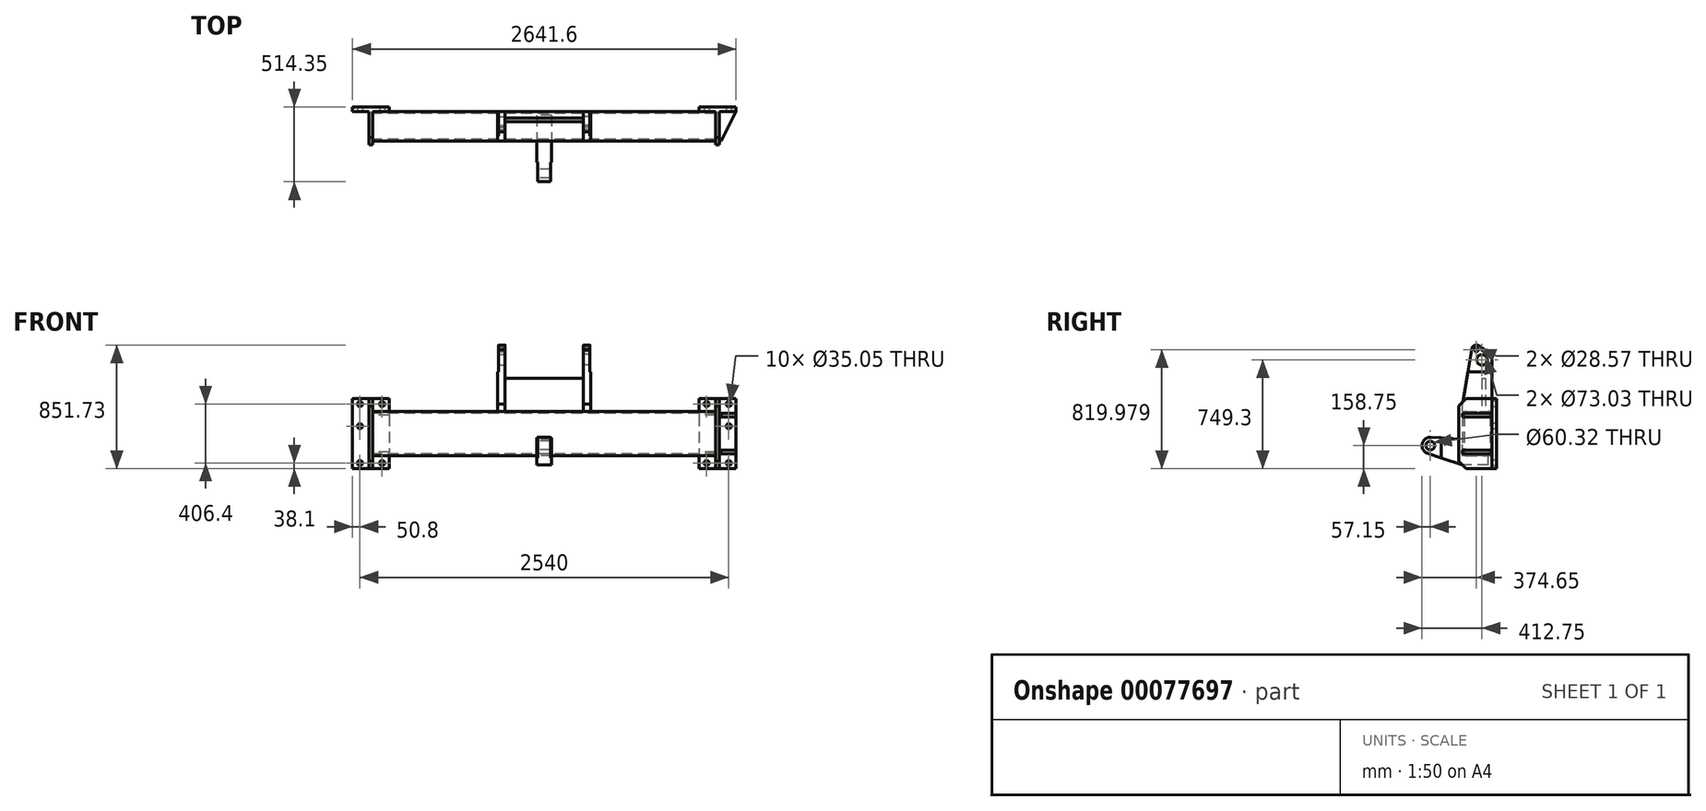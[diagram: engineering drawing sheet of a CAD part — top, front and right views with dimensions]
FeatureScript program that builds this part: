
annotation { "Feature Type Name" : "Feature", "Feature Type Description" : "" }
export const myFeature = defineFeature(function(context is Context, id is Id, definition is map)
    precondition{}
    {
        {
            var Q0;
            Q0=qCreatedBy(makeId("Right.planeOp"),FACE);
            var sketch = newSketch(context, id + "F0", { "sketchPlane" : qUnion([Q0])});
            skLineSegment(sketch, "E0.bottom", {"start": v(-76.2, 152.4) * mm, "end": v(76.2, 152.4) * mm});
            skLineSegment(sketch, "E0.top", {"start": v(-76.2, -152.4) * mm, "end": v(76.2, -152.4) * mm});
            skLineSegment(sketch, "E0.left", {"start": v(-101.6, 127) * mm, "end": v(-101.6, -127) * mm});
            skLineSegment(sketch, "E0.right", {"start": v(101.6, 127) * mm, "end": v(101.6, -127) * mm});
            skPoint(sketch, "E0.middle", {"position": v(0, 0) * mm});
            skPoint(sketch, "E1.visualSharp", {"position": v(-101.6, 152.4) * mm});
            skArc(sketch, "E1.filletArc", {"start": v(-76.2, 152.4) * mm, "mid": v(-94.16, 144.96) * mm, "end": v(-101.6, 127) * mm});
            skPoint(sketch, "E2.visualSharp", {"position": v(101.6, 152.4) * mm});
            skArc(sketch, "E2.filletArc", {"start": v(101.6, 127) * mm, "mid": v(94.16, 144.96) * mm, "end": v(76.2, 152.4) * mm});
            skPoint(sketch, "E3.visualSharp", {"position": v(101.6, -152.4) * mm});
            skArc(sketch, "E3.filletArc", {"start": v(76.2, -152.4) * mm, "mid": v(94.16, -144.96) * mm, "end": v(101.6, -127) * mm});
            skPoint(sketch, "E4.visualSharp", {"position": v(-101.6, -152.4) * mm});
            skArc(sketch, "E4.filletArc", {"start": v(-101.6, -127) * mm, "mid": v(-94.16, -144.96) * mm, "end": v(-76.2, -152.4) * mm});
            skArc(sketch, "E5.0", {"start": v(-76.2, 139.7) * mm, "mid": v(-85.18, 135.98) * mm, "end": v(-88.9, 127) * mm});
            skLineSegment(sketch, "E5.1", {"start": v(-88.9, 127) * mm, "end": v(-88.9, -127) * mm});
            skLineSegment(sketch, "E5.2", {"start": v(-76.2, 139.7) * mm, "end": v(76.2, 139.7) * mm});
            skArc(sketch, "E5.3", {"start": v(-88.9, -127) * mm, "mid": v(-85.18, -135.98) * mm, "end": v(-76.2, -139.7) * mm});
            skArc(sketch, "E5.4", {"start": v(88.9, 127) * mm, "mid": v(85.18, 135.98) * mm, "end": v(76.2, 139.7) * mm});
            skLineSegment(sketch, "E5.5", {"start": v(88.9, 127) * mm, "end": v(88.9, -127) * mm});
            skArc(sketch, "E5.6", {"start": v(76.2, -139.7) * mm, "mid": v(85.18, -135.98) * mm, "end": v(88.9, -127) * mm});
            skLineSegment(sketch, "E5.7", {"start": v(-76.2, -139.7) * mm, "end": v(76.2, -139.7) * mm});
            skSolve(sketch);
        }
        {
            var Q0;
            Q0 = qSketchRegion(id + "F0", true);
            extrude(context, id + "F1", {"entities" : qUnion([Q0]), "endBound" : BoundingType.SYMMETRIC, "depth" : 2362.2 * mm});
        }
        {
            var Q0;
            Q0=makeQuery(id+"F1.opExtrude","CAP_FACE",FACE,{"disambiguationData":[OSD([sQuery(id+"F0.wireOp",EDGE,"E0.bottom"),sQuery(id+"F0.wireOp",EDGE,"E0.top"),sQuery(id+"F0.wireOp",EDGE,"E0.left"),sQuery(id+"F0.wireOp",EDGE,"E0.right"),sQuery(id+"F0.wireOp",EDGE,"E1.filletArc"),sQuery(id+"F0.wireOp",EDGE,"E2.filletArc"),sQuery(id+"F0.wireOp",EDGE,"E3.filletArc"),sQuery(id+"F0.wireOp",EDGE,"E4.filletArc"),sQuery(id+"F0.wireOp",EDGE,"E5.0"),sQuery(id+"F0.wireOp",EDGE,"E5.1"),sQuery(id+"F0.wireOp",EDGE,"E5.2"),sQuery(id+"F0.wireOp",EDGE,"E5.3"),sQuery(id+"F0.wireOp",EDGE,"E5.4"),sQuery(id+"F0.wireOp",EDGE,"E5.5"),sQuery(id+"F0.wireOp",EDGE,"E5.6"),sQuery(id+"F0.wireOp",EDGE,"E5.7")])],"isStart":false});
            var sketch = newSketch(context, id + "F2", { "sketchPlane" : qUnion([Q0])});
            skLineSegment(sketch, "E6.0", {"start": v(-127, -241.3) * mm, "end": v(101.6, -241.3) * mm});
            skLineSegment(sketch, "E7.0", {"start": v(-127, 241.3) * mm, "end": v(101.6, 241.3) * mm});
            skLineSegment(sketch, "E8.0", {"start": v(101.6, 241.3) * mm, "end": v(101.6, -241.3) * mm});
            skPoint(sketch, "E9.orphan", {"position": v(101.6, 127) * mm});
            skPoint(sketch, "E10.orphan", {"position": v(101.6, -127) * mm});
            skLineSegment(sketch, "E11.0", {"start": v(-127, 241.3) * mm, "end": v(-127, -241.3) * mm});
            skSolve(sketch);
        }
        {
            var Q0;
            Q0 = qSketchRegion(id + "F2", true);
            extrude(context, id + "F3", {"entities" : qUnion([Q0]), "depth" : 25.4 * mm});
        }
        {
            var Q0;
            Q0=makeQuery(id+"F3.opExtrude","SWEPT_EDGE",EDGE,{"disambiguationData":[OSD([sQuery(id+"F2.wireOp",EDGE,"E7.0"),sQuery(id+"F2.wireOp",EDGE,"E11.0")])]});
            var Q1;
            Q1=makeQuery(id+"F3.opExtrude","SWEPT_EDGE",EDGE,{"disambiguationData":[OSD([sQuery(id+"F2.wireOp",EDGE,"E6.0"),sQuery(id+"F2.wireOp",EDGE,"E11.0")])]});
            chamfer(context, id + "F4", {"entities" : qUnion([Q0, Q1]), "width" : 50.8 * mm, "tangentPropagation" : true});
        }
        {
            var Q0;
            Q0=makeQuery(id+"F3.opExtrude","SWEPT_FACE",FACE,{"disambiguationData":[OSD([sQuery(id+"F2.wireOp",EDGE,"E8.0")])]});
            var sketch = newSketch(context, id + "F5", { "sketchPlane" : qUnion([Q0])});
            skLineSegment(sketch, "E12", {"start": v(-1193.8, 241.3) * mm, "end": v(-1193.8, -241.3) * mm, "construction": true});
            skLineSegment(sketch, "E13.bottom", {"start": v(-1320.8, 241.3) * mm, "end": v(-1066.8, 241.3) * mm});
            skLineSegment(sketch, "E13.top", {"start": v(-1320.8, -241.3) * mm, "end": v(-1066.8, -241.3) * mm});
            skLineSegment(sketch, "E13.left", {"start": v(-1320.8, 241.3) * mm, "end": v(-1320.8, -241.3) * mm});
            skLineSegment(sketch, "E13.right", {"start": v(-1066.8, 241.3) * mm, "end": v(-1066.8, -241.3) * mm});
            skPoint(sketch, "E13.middle", {"position": v(-1193.8, 0) * mm});
            skLineSegment(sketch, "E14", {"start": v(-1320.8, 0) * mm, "end": v(-1066.8, 0) * mm, "construction": true});
            skLineSegment(sketch, "E15.0", {"start": v(-1320.8, 203.2) * mm, "end": v(-1066.8, 203.2) * mm, "construction": true});
            skLineSegment(sketch, "E16.0", {"start": v(-1320.8, -203.2) * mm, "end": v(-1066.8, -203.2) * mm, "construction": true});
            skLineSegment(sketch, "E17.0", {"start": v(-1320.8, 50.8) * mm, "end": v(-1066.8, 50.8) * mm, "construction": true});
            skLineSegment(sketch, "E18.0", {"start": v(-1270, 241.3) * mm, "end": v(-1270, -241.3) * mm, "construction": true});
            skLineSegment(sketch, "E19.0", {"start": v(-1117.6, 241.3) * mm, "end": v(-1117.6, -241.3) * mm, "construction": true});
            skCircle(sketch, "E20", {"center": v(-1270, 203.2) * mm, "radius": 17.53 * mm});
            skCircle(sketch, "E21", {"center": v(-1117.6, 203.2) * mm, "radius": 17.53 * mm});
            skCircle(sketch, "E22", {"center": v(-1270, 50.8) * mm, "radius": 17.53 * mm});
            skCircle(sketch, "E23", {"center": v(-1270, -203.2) * mm, "radius": 17.53 * mm});
            skCircle(sketch, "E24", {"center": v(-1117.6, -203.2) * mm, "radius": 17.53 * mm});
            skSolve(sketch);
        }
        {
            var Q0;
            Q0 = qSketchRegion(id + "F5", true);
            extrude(context, id + "F6", {"entities" : qUnion([Q0]), "depth" : 31.75 * mm});
        }
        {
            var Q0;
            Q0=makeQuery(id+"F6.opExtrude","CAP_FACE",FACE,{"disambiguationData":[OSD([sQuery(id+"F5.wireOp",EDGE,"E13.bottom"),sQuery(id+"F5.wireOp",EDGE,"E13.top"),sQuery(id+"F5.wireOp",EDGE,"E13.left"),sQuery(id+"F5.wireOp",EDGE,"E13.right"),sQuery(id+"F5.wireOp",EDGE,"E20"),sQuery(id+"F5.wireOp",EDGE,"E21"),sQuery(id+"F5.wireOp",EDGE,"E22"),sQuery(id+"F5.wireOp",EDGE,"E23"),sQuery(id+"F5.wireOp",EDGE,"E24")])],"isStart":true});
            var sketch = newSketch(context, id + "F7", { "sketchPlane" : qUnion([Q0])});
            skLineSegment(sketch, "E25.0", {"start": v(1320.8, -241.3) * mm, "end": v(1066.8, -241.3) * mm});
            skLineSegment(sketch, "E26.0", {"start": v(1206.5, 190.5) * mm, "end": v(1206.5, -190.5) * mm});
            skLineSegment(sketch, "E27.0", {"start": v(1320.8, -139.7) * mm, "end": v(1206.5, -139.7) * mm});
            skLineSegment(sketch, "E28.0", {"start": v(1320.8, -114.3) * mm, "end": v(1206.5, -114.3) * mm});
            skLineSegment(sketch, "E29.0", {"start": v(1320.8, 114.3) * mm, "end": v(1206.5, 114.3) * mm});
            skLineSegment(sketch, "E30.0", {"start": v(1320.8, 139.7) * mm, "end": v(1206.5, 139.7) * mm});
            skLineSegment(sketch, "E31", {"start": v(1320.8, 139.7) * mm, "end": v(1320.8, 114.3) * mm});
            skLineSegment(sketch, "E32", {"start": v(1320.8, -114.3) * mm, "end": v(1320.8, -139.7) * mm});
            skSolve(sketch);
        }
        {
            var Q0;
            Q0 = qSketchRegion(id + "F7", true);
            extrude(context, id + "F8", {"entities" : qUnion([Q0]), "depth" : 203.2 * mm});
        }
        {
            var Q0;
            Q0=makeQuery(id+"F8.opExtrude","SWEPT_FACE",FACE,{"disambiguationData":[OSD([sQuery(id+"F7.wireOp",EDGE,"E30.0")])]});
            var sketch = newSketch(context, id + "F9", { "sketchPlane" : qUnion([Q0])});
            skLineSegment(sketch, "E33.0", {"start": v(1206.5, -101.6) * mm, "end": v(1206.5, 101.6) * mm});
            skLineSegment(sketch, "E34.0", {"start": v(1320.8, -101.6) * mm, "end": v(1206.5, -101.6) * mm});
            skLineSegment(sketch, "E35.0", {"start": v(1320.8, -101.6) * mm, "end": v(1320.8, 101.6) * mm});
            skLineSegment(sketch, "E36.0", {"start": v(1219.2, -101.6) * mm, "end": v(1219.2, 101.6) * mm, "construction": true});
            skLineSegment(sketch, "E37", {"start": v(1219.2, -101.6) * mm, "end": v(1320.8, 101.6) * mm});
            skSolve(sketch);
        }
        {
            var Q0;
            Q0 = qSketchRegion(id + "F9", true);
            extrude(context, id + "F10", {"entities" : qUnion([Q0]), "operationType" : NewBodyOperationType.REMOVE, "endBound" : BoundingType.THROUGH_ALL, "oppositeDirection" : true, "depth" : 25.4 * mm});
        }
        {
            var Q0;
            Q0=makeQuery(id+"F3.opExtrude","SWEPT_BODY",BODY,{"disambiguationData":[OSD([sQuery(id+"F2.wireOp",EDGE,"E6.0"),sQuery(id+"F2.wireOp",EDGE,"E7.0"),sQuery(id+"F2.wireOp",EDGE,"E8.0"),sQuery(id+"F2.wireOp",EDGE,"E11.0")])]});
            var Q1;
            Q1=makeQuery(id+"F6.opExtrude","SWEPT_BODY",BODY,{"disambiguationData":[OSD([sQuery(id+"F5.wireOp",EDGE,"E13.bottom"),sQuery(id+"F5.wireOp",EDGE,"E13.top"),sQuery(id+"F5.wireOp",EDGE,"E13.left"),sQuery(id+"F5.wireOp",EDGE,"E13.right"),sQuery(id+"F5.wireOp",EDGE,"E20"),sQuery(id+"F5.wireOp",EDGE,"E21"),sQuery(id+"F5.wireOp",EDGE,"E22"),sQuery(id+"F5.wireOp",EDGE,"E23"),sQuery(id+"F5.wireOp",EDGE,"E24")])]});
            var Q2;
            Q2=qCreatedBy(makeId("Right.planeOp"),FACE);
            mirror(context, id + "F11", {"entities" : qUnion([Q0, Q1]), "mirrorPlane" : qUnion([Q2])});
        }
        {
            var Q0;
            Q0=makeQuery(id+"F1.opExtrude","SWEPT_BODY",BODY,{"disambiguationData":[OSD([sQuery(id+"F0.wireOp",EDGE,"E0.bottom"),sQuery(id+"F0.wireOp",EDGE,"E0.top"),sQuery(id+"F0.wireOp",EDGE,"E0.left"),sQuery(id+"F0.wireOp",EDGE,"E0.right"),sQuery(id+"F0.wireOp",EDGE,"E1.filletArc"),sQuery(id+"F0.wireOp",EDGE,"E2.filletArc"),sQuery(id+"F0.wireOp",EDGE,"E3.filletArc"),sQuery(id+"F0.wireOp",EDGE,"E4.filletArc"),sQuery(id+"F0.wireOp",EDGE,"E5.0"),sQuery(id+"F0.wireOp",EDGE,"E5.1"),sQuery(id+"F0.wireOp",EDGE,"E5.2"),sQuery(id+"F0.wireOp",EDGE,"E5.3"),sQuery(id+"F0.wireOp",EDGE,"E5.4"),sQuery(id+"F0.wireOp",EDGE,"E5.5"),sQuery(id+"F0.wireOp",EDGE,"E5.6"),sQuery(id+"F0.wireOp",EDGE,"E5.7")])]});
            var Q1;
            Q1=makeQuery(id+"F3.opExtrude","SWEPT_BODY",BODY,{"disambiguationData":[OSD([sQuery(id+"F2.wireOp",EDGE,"E6.0"),sQuery(id+"F2.wireOp",EDGE,"E7.0"),sQuery(id+"F2.wireOp",EDGE,"E8.0"),sQuery(id+"F2.wireOp",EDGE,"E11.0")])]});
            var Q2;
            Q2=makeQuery(id+"F11.opPattern","COPY",BODY,{"derivedFrom":makeQuery(id+"F3.opExtrude","SWEPT_BODY",BODY,{"disambiguationData":[OSD([sQuery(id+"F2.wireOp",EDGE,"E6.0"),sQuery(id+"F2.wireOp",EDGE,"E7.0"),sQuery(id+"F2.wireOp",EDGE,"E8.0"),sQuery(id+"F2.wireOp",EDGE,"E11.0")])]}),"instanceName":"1"});
            var Q3;
            Q3=makeQuery(id+"F11.opPattern","COPY",BODY,{"derivedFrom":makeQuery(id+"F6.opExtrude","SWEPT_BODY",BODY,{"disambiguationData":[OSD([sQuery(id+"F5.wireOp",EDGE,"E13.bottom"),sQuery(id+"F5.wireOp",EDGE,"E13.top"),sQuery(id+"F5.wireOp",EDGE,"E13.left"),sQuery(id+"F5.wireOp",EDGE,"E13.right"),sQuery(id+"F5.wireOp",EDGE,"E20"),sQuery(id+"F5.wireOp",EDGE,"E21"),sQuery(id+"F5.wireOp",EDGE,"E22"),sQuery(id+"F5.wireOp",EDGE,"E23"),sQuery(id+"F5.wireOp",EDGE,"E24")])]}),"instanceName":"1"});
            var Q4;
            Q4=makeQuery(id+"F6.opExtrude","SWEPT_BODY",BODY,{"disambiguationData":[OSD([sQuery(id+"F5.wireOp",EDGE,"E13.bottom"),sQuery(id+"F5.wireOp",EDGE,"E13.top"),sQuery(id+"F5.wireOp",EDGE,"E13.left"),sQuery(id+"F5.wireOp",EDGE,"E13.right"),sQuery(id+"F5.wireOp",EDGE,"E20"),sQuery(id+"F5.wireOp",EDGE,"E21"),sQuery(id+"F5.wireOp",EDGE,"E22"),sQuery(id+"F5.wireOp",EDGE,"E23"),sQuery(id+"F5.wireOp",EDGE,"E24")])]});
            booleanBodies(context, id + "F12", {"operationType" : BooleanOperationType.UNION, "tools" : qUnion([Q0, Q1, Q2, Q3, Q4])});
        }
        {
            var Q0;
            Q0=qCreatedBy(makeId("Right.planeOp"),FACE);
            var sketch = newSketch(context, id + "F13", { "sketchPlane" : qUnion([Q0])});
            skLineSegment(sketch, "E38.0", {"start": v(31.75, 152.4) * mm, "end": v(57.15, 152.4) * mm});
            skLineSegment(sketch, "E39.0", {"start": v(101.6, 241.3) * mm, "end": v(101.6, 152.4) * mm});
            skPoint(sketch, "E40.orphan", {"position": v(76.2, 152.4) * mm});
            skPoint(sketch, "E41.orphan", {"position": v(101.6, 127) * mm});
            skLineSegment(sketch, "E42.0", {"start": v(31.75, 381) * mm, "end": v(57.15, 381) * mm});
            skLineSegment(sketch, "E43.0", {"start": v(57.15, 381) * mm, "end": v(57.15, 152.4) * mm});
            skLineSegment(sketch, "E44.0", {"start": v(31.75, 381) * mm, "end": v(31.75, 152.4) * mm});
            skPoint(sketch, "E45.orphan", {"position": v(-76.2, 152.4) * mm});
            skSolve(sketch);
        }
        {
            var Q0;
            Q0 = qSketchRegion(id + "F13", true);
            extrude(context, id + "F14", {"entities" : qUnion([Q0]), "endBound" : BoundingType.SYMMETRIC, "depth" : 539.75 * mm});
        }
        {
            var Q0;
            Q0=makeQuery(id+"F14.opExtrude","CAP_FACE",FACE,{"disambiguationData":[OSD([sQuery(id+"F13.wireOp",EDGE,"E38.0"),sQuery(id+"F13.wireOp",EDGE,"E42.0"),sQuery(id+"F13.wireOp",EDGE,"E43.0"),sQuery(id+"F13.wireOp",EDGE,"E44.0")])],"isStart":false});
            var sketch = newSketch(context, id + "F15", { "sketchPlane" : qUnion([Q0])});
            skLineSegment(sketch, "E46.0.0", {"start": v(31.75, 381) * mm, "end": v(31.75, 152.4) * mm, "construction": true});
            skLineSegment(sketch, "E46.0.1", {"start": v(31.75, 152.4) * mm, "end": v(57.15, 152.4) * mm, "construction": true});
            skLineSegment(sketch, "E46.0.2", {"start": v(57.15, 152.4) * mm, "end": v(57.15, 381) * mm, "construction": true});
            skLineSegment(sketch, "E46.0.3", {"start": v(57.15, 381) * mm, "end": v(31.75, 381) * mm, "construction": true});
            skLineSegment(sketch, "E47.0", {"start": v(101.6, 152.4) * mm, "end": v(101.6, 508) * mm});
            skLineSegment(sketch, "E48.0", {"start": v(-101.6, 152.4) * mm, "end": v(-101.6, 203.2) * mm});
            skLineSegment(sketch, "E49", {"start": v(-101.6, 152.4) * mm, "end": v(101.6, 152.4) * mm});
            skLineSegment(sketch, "E50.0", {"start": v(-76.2, -241.3) * mm, "end": v(101.6, -241.3) * mm, "construction": true});
            skLineSegment(sketch, "E51.0", {"start": v(-76.2, 508) * mm, "end": v(101.6, 508) * mm, "construction": true});
            skLineSegment(sketch, "E52.0", {"start": v(31.75, 152.4) * mm, "end": v(31.75, 504) * mm, "construction": true});
            skLineSegment(sketch, "E53", {"start": v(31.75, 504) * mm, "end": v(-262.89, 504) * mm, "construction": true});
            skLineSegment(sketch, "E54.0", {"start": v(31.75, 578.68) * mm, "end": v(-262.89, 578.68) * mm, "construction": true});
            skLineSegment(sketch, "E55", {"start": v(31.75, 504) * mm, "end": v(31.75, 730.25) * mm, "construction": true});
            skLineSegment(sketch, "E56.0", {"start": v(-6.35, 508) * mm, "end": v(-6.35, 730.25) * mm, "construction": true});
            skArc(sketch, "E57", {"start": v(11.1, 605.2) * mm, "mid": v(-21.42, 606.63) * mm, "end": v(-38.1, 578.68) * mm});
            skLineSegment(sketch, "E58", {"start": v(11.1, 605.2) * mm, "end": v(70.15, 566.35) * mm});
            skArc(sketch, "E59.trimOffspring", {"start": v(25.38, 577.56) * mm, "mid": v(25.4, 578.12) * mm, "end": v(25.4, 578.68) * mm});
            skArc(sketch, "E60.trimOffspring", {"start": v(31.75, 577.85) * mm, "mid": v(28.56, 577.78) * mm, "end": v(25.38, 577.56) * mm});
            skArc(sketch, "E61.trimOffspring", {"start": v(101.6, 508) * mm, "mid": v(93.24, 541.14) * mm, "end": v(70.15, 566.35) * mm});
            skLineSegment(sketch, "E62", {"start": v(-38.1, 578.68) * mm, "end": v(-101.6, 203.2) * mm});
            skCircle(sketch, "E63", {"center": v(31.75, 508) * mm, "radius": 36.51 * mm});
            skCircle(sketch, "E64", {"center": v(-6.35, 578.68) * mm, "radius": 14.29 * mm});
            skSolve(sketch);
        }
        {
            var Q0;
            Q0=makeQuery(id+"F15.imprint","IMPRINT",FACE,{"disambiguationData":[TD([[makeQuery(id+"F15.imprint","IMPRINT",EDGE,{"derivedFrom":sQuery(id+"F15.wireOp",EDGE,"E57")}),1.0]])]});
            var Q1;
            Q1=makeQuery(id+"F15.imprint","IMPRINT",FACE,{"disambiguationData":[TD([[makeQuery(id+"F15.imprint","IMPRINT",EDGE,{"derivedFrom":makeQuery(id+"F14.opExtrude","CAP_EDGE",EDGE,{"disambiguationData":[OSD([sQuery(id+"F13.wireOp",EDGE,"E42.0")])],"isStart":false})}),-1.0]])]});
            extrude(context, id + "F16", {"entities" : qUnion([Q0, Q1]), "depth" : 50.8 * mm});
        }
        {
            var Q0;
            Q0=makeQuery(id+"F16.opExtrude","CAP_FACE",FACE,{"disambiguationData":[OSD([sQuery(id+"F15.wireOp",EDGE,"E57"),sQuery(id+"F15.wireOp",EDGE,"E58"),sQuery(id+"F15.wireOp",EDGE,"E61.trimOffspring"),sQuery(id+"F15.wireOp",EDGE,"E49"),sQuery(id+"F15.wireOp",EDGE,"E48.0"),sQuery(id+"F15.wireOp",EDGE,"E47.0"),sQuery(id+"F15.wireOp",EDGE,"E62"),sQuery(id+"F15.wireOp",EDGE,"E63"),sQuery(id+"F15.wireOp",EDGE,"E64")])],"isStart":false});
            var sketch = newSketch(context, id + "F17", { "sketchPlane" : qUnion([Q0])});
            skLineSegment(sketch, "E65", {"start": v(31.75, 508) * mm, "end": v(-156.48, 508) * mm, "construction": true});
            skLineSegment(sketch, "E66.0", {"start": v(31.75, 425.45) * mm, "end": v(-156.48, 425.45) * mm, "construction": true});
            skLineSegment(sketch, "E67.bottom", {"start": v(-156.48, 425.45) * mm, "end": v(204.9, 425.45) * mm});
            skLineSegment(sketch, "E67.top", {"start": v(-156.48, 748.84) * mm, "end": v(204.9, 748.84) * mm});
            skLineSegment(sketch, "E67.left", {"start": v(-156.48, 425.45) * mm, "end": v(-156.48, 748.84) * mm});
            skLineSegment(sketch, "E67.right", {"start": v(204.9, 425.45) * mm, "end": v(204.9, 748.84) * mm});
            skSolve(sketch);
        }
        {
            var Q0;
            Q0 = qSketchRegion(id + "F17", true);
            extrude(context, id + "F18", {"entities" : qUnion([Q0]), "operationType" : NewBodyOperationType.REMOVE, "oppositeDirection" : true, "depth" : 6.35 * mm});
        }
        {
            var Q0;
            Q0=makeQuery(id+"F16.opExtrude","SWEPT_BODY",BODY,{"disambiguationData":[OSD([sQuery(id+"F15.wireOp",EDGE,"E57"),sQuery(id+"F15.wireOp",EDGE,"E58"),sQuery(id+"F15.wireOp",EDGE,"E61.trimOffspring"),sQuery(id+"F15.wireOp",EDGE,"E49"),sQuery(id+"F15.wireOp",EDGE,"E48.0"),sQuery(id+"F15.wireOp",EDGE,"E47.0"),sQuery(id+"F15.wireOp",EDGE,"E62"),sQuery(id+"F15.wireOp",EDGE,"E63"),sQuery(id+"F15.wireOp",EDGE,"E64")])]});
            var Q1;
            Q1=qCreatedBy(makeId("Right.planeOp"),FACE);
            mirror(context, id + "F19", {"entities" : qUnion([Q0]), "mirrorPlane" : qUnion([Q1])});
        }
        {
            var Q0;
            Q0=qCreatedBy(makeId("Right.planeOp"),FACE);
            var sketch = newSketch(context, id + "F20", { "sketchPlane" : qUnion([Q0])});
            skLineSegment(sketch, "E68.0", {"start": v(76.2, -215.9) * mm, "end": v(-101.6, -215.9) * mm});
            skLineSegment(sketch, "E69.0", {"start": v(-101.6, 127) * mm, "end": v(-101.6, -127) * mm, "construction": true});
            skLineSegment(sketch, "E70.0", {"start": v(76.2, 127) * mm, "end": v(76.2, -82.55) * mm, "construction": true});
            skLineSegment(sketch, "E71.0", {"start": v(133.35, 241.3) * mm, "end": v(133.35, -241.3) * mm, "construction": true});
            skLineSegment(sketch, "E72.0", {"start": v(-323.85, 241.3) * mm, "end": v(-323.85, -241.3) * mm, "construction": true});
            skLineSegment(sketch, "E73.0", {"start": v(-323.85, -241.3) * mm, "end": v(101.6, -241.3) * mm, "construction": true});
            skPoint(sketch, "E74.orphan", {"position": v(-76.2, -241.3) * mm});
            skLineSegment(sketch, "E75.0", {"start": v(-323.85, -82.55) * mm, "end": v(101.6, -82.55) * mm, "construction": true});
            skArc(sketch, "E76", {"start": v(-320.57, -25.5) * mm, "mid": v(-380.98, -80.9) * mm, "end": v(-323.85, -139.7) * mm});
            skCircle(sketch, "E77", {"center": v(-323.85, -82.55) * mm, "radius": 30.16 * mm});
            skLineSegment(sketch, "E78.0", {"start": v(101.6, -38.1) * mm, "end": v(-101.6, -38.1) * mm, "construction": true});
            skLineSegment(sketch, "E79", {"start": v(-101.6, -38.1) * mm, "end": v(-320.57, -25.5) * mm});
            skLineSegment(sketch, "E80", {"start": v(-101.6, -215.9) * mm, "end": v(-341.72, -136.83) * mm});
            skLineSegment(sketch, "E81.0", {"start": v(-76.2, -152.4) * mm, "end": v(76.2, -152.4) * mm, "construction": true});
            skLineSegment(sketch, "E82", {"start": v(-101.6, -38.1) * mm, "end": v(-101.6, -139.7) * mm});
            skLineSegment(sketch, "E83.trimOffspring", {"start": v(76.2, -152.4) * mm, "end": v(76.2, -215.9) * mm, "construction": true});
            skLineSegment(sketch, "E84", {"start": v(76.2, -215.9) * mm, "end": v(76.2, -152.4) * mm});
            skLineSegment(sketch, "E85", {"start": v(76.2, -152.4) * mm, "end": v(-101.6, -152.4) * mm});
            skLineSegment(sketch, "E86", {"start": v(-101.6, -152.4) * mm, "end": v(-101.6, -127) * mm});
            skSolve(sketch);
        }
        {
            var Q0;
            Q0 = qSketchRegion(id + "F20", true);
            extrude(context, id + "F21", {"entities" : qUnion([Q0]), "endBound" : BoundingType.SYMMETRIC, "depth" : 101.6 * mm});
        }
        {
            var Q0;
            Q0=makeQuery(id+"F21.opExtrude","CAP_FACE",FACE,{"disambiguationData":[OSD([sQuery(id+"F20.wireOp",EDGE,"E68.0"),sQuery(id+"F20.wireOp",EDGE,"E76"),sQuery(id+"F20.wireOp",EDGE,"E77"),sQuery(id+"F20.wireOp",EDGE,"E79"),sQuery(id+"F20.wireOp",EDGE,"E80"),sQuery(id+"F20.wireOp",EDGE,"E82"),sQuery(id+"F20.wireOp",EDGE,"E84"),sQuery(id+"F20.wireOp",EDGE,"E85"),sQuery(id+"F20.wireOp",EDGE,"E86")])],"isStart":false});
            var sketch = newSketch(context, id + "F22", { "sketchPlane" : qUnion([Q0])});
            skLineSegment(sketch, "E87", {"start": v(-323.85, -82.55) * mm, "end": v(-323.85, -212.97) * mm, "construction": true});
            skLineSegment(sketch, "E88.0", {"start": v(-247.65, -82.55) * mm, "end": v(-247.65, -212.97) * mm});
            skLineSegment(sketch, "E89.bottom", {"start": v(-247.65, -212.97) * mm, "end": v(-439.1, -212.97) * mm});
            skLineSegment(sketch, "E89.top", {"start": v(-247.65, 21.78) * mm, "end": v(-439.1, 21.78) * mm});
            skLineSegment(sketch, "E89.left", {"start": v(-247.65, -212.97) * mm, "end": v(-247.65, 21.78) * mm});
            skLineSegment(sketch, "E89.right", {"start": v(-439.1, -212.97) * mm, "end": v(-439.1, 21.78) * mm});
            skSolve(sketch);
        }
        {
            var Q0;
            Q0 = qSketchRegion(id + "F22", true);
            extrude(context, id + "F23", {"entities" : qUnion([Q0]), "oppositeDirection" : true, "depth" : 6.35 * mm});
        }
        {
            var Q0;
            Q0=makeQuery(id+"F23.opExtrude","SWEPT_BODY",BODY,{"disambiguationData":[OSD([sQuery(id+"F22.wireOp",EDGE,"E89.bottom"),sQuery(id+"F22.wireOp",EDGE,"E89.top"),sQuery(id+"F22.wireOp",EDGE,"E89.left"),sQuery(id+"F22.wireOp",EDGE,"E89.right")])]});
            var Q1;
            Q1=qCreatedBy(makeId("Right.planeOp"),FACE);
            mirror(context, id + "F24", {"entities" : qUnion([Q0]), "mirrorPlane" : qUnion([Q1])});
        }
        {
            var Q0;
            Q0=makeQuery(id+"F24.opPattern","COPY",BODY,{"derivedFrom":makeQuery(id+"F23.opExtrude","SWEPT_BODY",BODY,{"disambiguationData":[OSD([sQuery(id+"F22.wireOp",EDGE,"E89.bottom"),sQuery(id+"F22.wireOp",EDGE,"E89.top"),sQuery(id+"F22.wireOp",EDGE,"E89.left"),sQuery(id+"F22.wireOp",EDGE,"E89.right")])]}),"instanceName":"1"});
            var Q1;
            Q1=makeQuery(id+"F23.opExtrude","SWEPT_BODY",BODY,{"disambiguationData":[OSD([sQuery(id+"F22.wireOp",EDGE,"E89.bottom"),sQuery(id+"F22.wireOp",EDGE,"E89.top"),sQuery(id+"F22.wireOp",EDGE,"E89.left"),sQuery(id+"F22.wireOp",EDGE,"E89.right")])]});
            var Q2;
            Q2=makeQuery(id+"F21.opExtrude","SWEPT_BODY",BODY,{"disambiguationData":[OSD([sQuery(id+"F20.wireOp",EDGE,"E68.0"),sQuery(id+"F20.wireOp",EDGE,"E76"),sQuery(id+"F20.wireOp",EDGE,"E77"),sQuery(id+"F20.wireOp",EDGE,"E79"),sQuery(id+"F20.wireOp",EDGE,"E80"),sQuery(id+"F20.wireOp",EDGE,"E82"),sQuery(id+"F20.wireOp",EDGE,"E84"),sQuery(id+"F20.wireOp",EDGE,"E85"),sQuery(id+"F20.wireOp",EDGE,"E86")])]});
            booleanBodies(context, id + "F25", {"operationType" : BooleanOperationType.SUBTRACTION, "tools" : qUnion([Q0, Q1]), "targets" : qUnion([Q2])});
        }
    });
